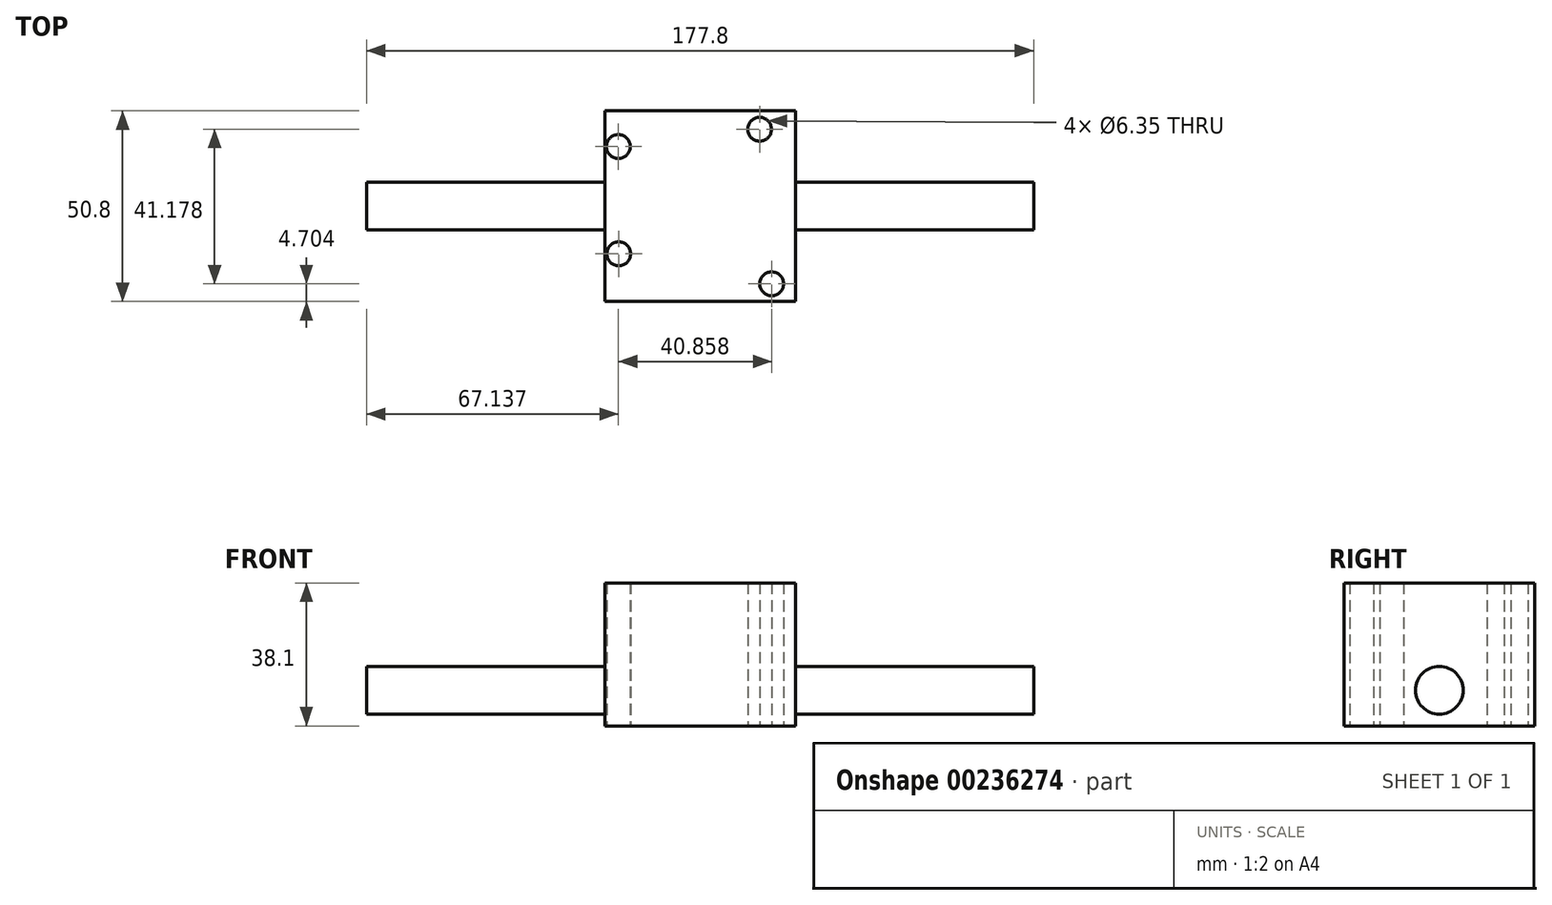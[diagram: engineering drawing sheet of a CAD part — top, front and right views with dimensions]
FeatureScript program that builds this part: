
annotation { "Feature Type Name" : "Feature", "Feature Type Description" : "" }
export const myFeature = defineFeature(function(context is Context, id is Id, definition is map)
    precondition{}
    {
        {
            var Q0;
            Q0=qCreatedBy(makeId("Top.planeOp"),FACE);
            var sketch = newSketch(context, id + "F0", { "sketchPlane" : qUnion([Q0])});
            skLineSegment(sketch, "E0.bottom", {"start": v(25.4, -25.4) * mm, "end": v(-25.4, -25.4) * mm});
            skLineSegment(sketch, "E0.top", {"start": v(25.4, 25.4) * mm, "end": v(-25.4, 25.4) * mm});
            skLineSegment(sketch, "E0.left", {"start": v(25.4, -25.4) * mm, "end": v(25.4, 25.4) * mm});
            skLineSegment(sketch, "E0.right", {"start": v(-25.4, -25.4) * mm, "end": v(-25.4, 25.4) * mm});
            skPoint(sketch, "E0.middle", {"position": v(0, 0) * mm});
            skCircle(sketch, "E1", {"center": v(-21.76, 15.87) * mm, "radius": 3.18 * mm});
            skCircle(sketch, "E2", {"center": v(15.88, 20.48) * mm, "radius": 3.18 * mm});
            skCircle(sketch, "E3", {"center": v(-21.66, -12.7) * mm, "radius": 3.18 * mm});
            skCircle(sketch, "E4", {"center": v(19.1, -20.7) * mm, "radius": 3.18 * mm});
            skSolve(sketch);
        }
        {
            var Q0;
            Q0=makeQuery(id+"F0.imprint","IMPRINT",FACE,{"disambiguationData":[TD([[makeQuery(id+"F0.imprint","IMPRINT",EDGE,{"derivedFrom":sQuery(id+"F0.wireOp",EDGE,"E0.bottom")}),-1.0]])]});
            extrude(context, id + "F1", {"entities" : qUnion([Q0]), "endBound" : BoundingType.SYMMETRIC, "depth" : 38.1 * mm});
        }
        {
            var Q0;
            Q0=qCreatedBy(makeId("Right.planeOp"),FACE);
            var sketch = newSketch(context, id + "F2", { "sketchPlane" : qUnion([Q0])});
            skCircle(sketch, "E5", {"center": v(0, -9.53) * mm, "radius": 6.35 * mm});
            skSolve(sketch);
        }
        {
            var Q0;
            Q0 = qSketchRegion(id + "F2", true);
            extrude(context, id + "F3", {"entities" : qUnion([Q0]), "operationType" : NewBodyOperationType.ADD, "endBound" : BoundingType.SYMMETRIC, "depth" : 177.8 * mm});
        }
    });
